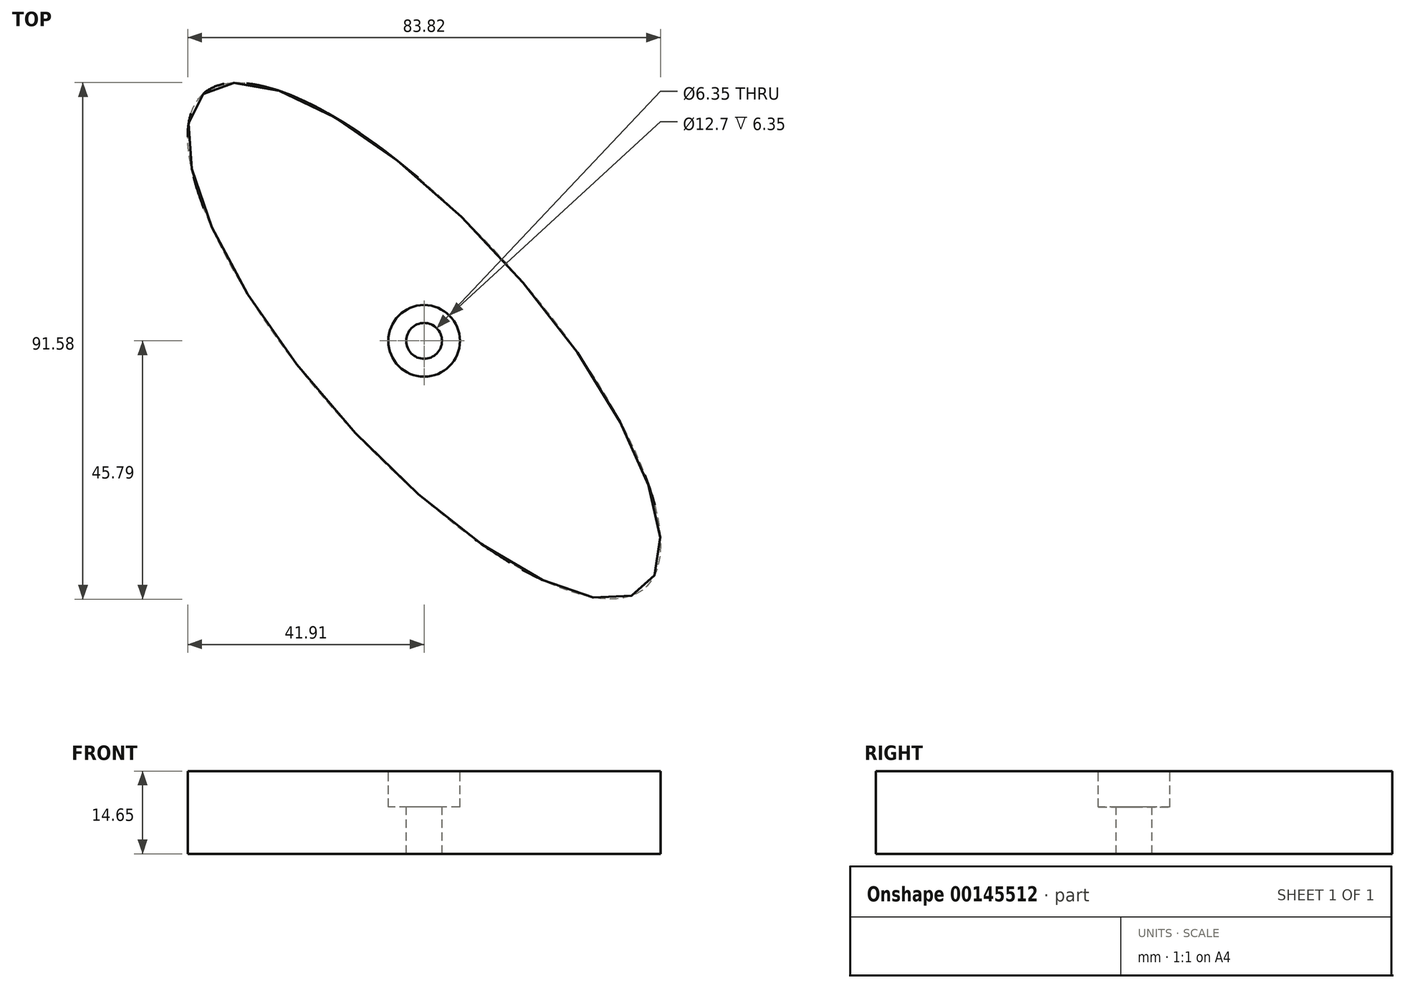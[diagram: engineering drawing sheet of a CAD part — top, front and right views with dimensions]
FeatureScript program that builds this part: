
annotation { "Feature Type Name" : "Feature", "Feature Type Description" : "" }
export const myFeature = defineFeature(function(context is Context, id is Id, definition is map)
    precondition{}
    {
        {
            var Q0;
            Q0=qCreatedBy(makeId("Top.planeOp"),FACE);
            var sketch = newSketch(context, id + "F0", { "sketchPlane" : qUnion([Q0])});
            skEllipse(sketch, "E0", {"center": v(0, 0) * mm, "majorRadius": 58.76 * mm, "minorRadius": 20.02 * mm, "majorAxis": v(-0.67, 0.75)});
            skSolve(sketch);
        }
        {
            var Q0;
            Q0=makeQuery(id+"F0.imprint","IMPRINT",FACE,{"disambiguationData":[TD([[makeQuery(id+"F0.imprint","IMPRINT",EDGE,{"derivedFrom":sQuery(id+"F0.wireOp",EDGE,"E0")}),1.0]])]});
            extrude(context, id + "F1", {"entities" : qUnion([Q0]), "depth" : 14.65 * mm});
        }
        {
            var Q1;
            Q1=makeQuery(id+"F1.opExtrude","CAP_FACE",FACE,{"disambiguationData":[OSD([sQuery(id+"F0.wireOp",EDGE,"E0")])],"isStart":false});
            var Q2;
            Q2=makeQuery(id+"F1.opExtrude","CAP_FACE",FACE,{"disambiguationData":[OSD([sQuery(id+"F0.wireOp",EDGE,"E0")])],"isStart":true});
            loft(context, id + "F2", {"operationType" : NewBodyOperationType.ADD, "sheetProfilesArray" : [{ "sheetProfileEntities" : qUnion([Q1]) }, { "sheetProfileEntities" : qUnion([Q2]) }]});
        }
        {
            var Q0;
            Q0=makeQuery(id+"F1.opExtrude","CAP_FACE",FACE,{"disambiguationData":[OSD([sQuery(id+"F0.wireOp",EDGE,"E0")])],"isStart":false});
            var sketch = newSketch(context, id + "F3", { "sketchPlane" : qUnion([Q0])});
            skCircle(sketch, "E1", {"center": v(0, 0) * mm, "radius": 5.75 * mm});
            skSolve(sketch);
        }
        {
            var Q0;
            Q0=sQuery(id+"F3.wireOp",VERTEX,"E1.center");
            var Q1;
            Q1=makeQuery(id+"F1.opExtrude","SWEPT_BODY",BODY,{"disambiguationData":[OSD([sQuery(id+"F0.wireOp",EDGE,"E0")])]});
            hole(context, id + "F4", {"style" : HoleStyle.C_BORE, "endStyle" : HoleEndStyle.THROUGH, "holeDiameter" : 6.35 * mm, "cBoreDiameter" : 12.7 * mm, "cBoreDepth" : 6.35 * mm, "locations" : qUnion([Q0]), "scope" : qUnion([Q1]), "isTappedThrough" : true});
        }
    });
